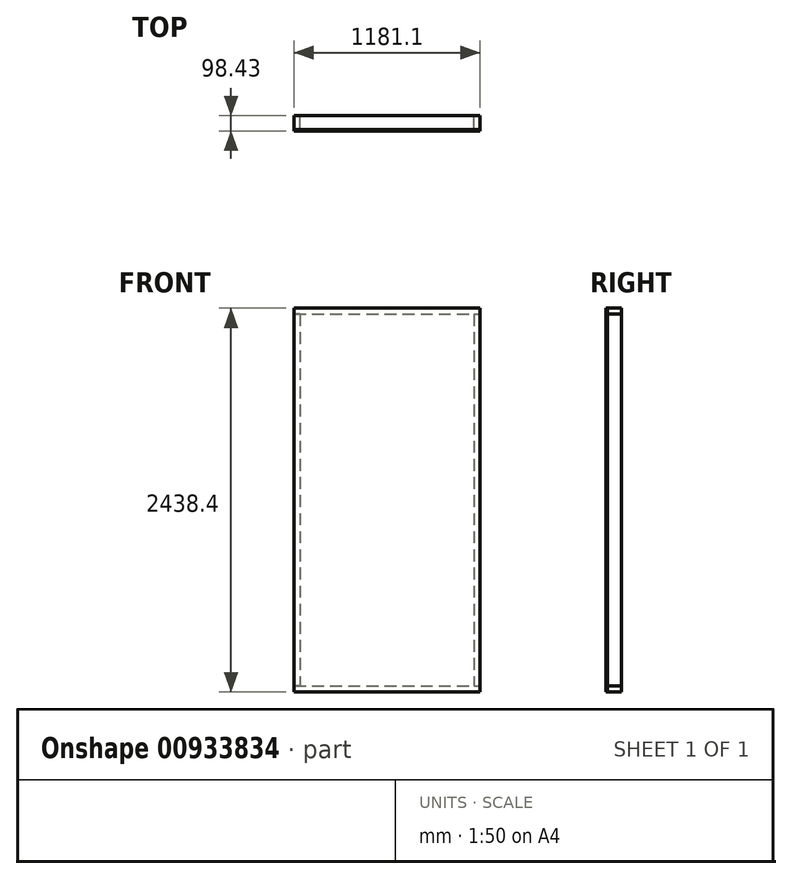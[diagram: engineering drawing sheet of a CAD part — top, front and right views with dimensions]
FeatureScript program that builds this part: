
annotation { "Feature Type Name" : "Feature", "Feature Type Description" : "" }
export const myFeature = defineFeature(function(context is Context, id is Id, definition is map)
    precondition{}
    {
        {
            var Q0;
            Q0=qCreatedBy(makeId("Front.planeOp"),FACE);
            var sketch = newSketch(context, id + "F0", { "sketchPlane" : qUnion([Q0])});
            skLineSegment(sketch, "E0.bottom", {"start": v(552.45, -1181.1) * mm, "end": v(-552.45, -1181.1) * mm, "construction": true});
            skLineSegment(sketch, "E0.top", {"start": v(552.45, 1181.1) * mm, "end": v(-552.45, 1181.1) * mm, "construction": true});
            skLineSegment(sketch, "E0.left", {"start": v(552.45, -1181.1) * mm, "end": v(552.45, 1181.1) * mm, "construction": true});
            skLineSegment(sketch, "E0.right", {"start": v(-552.45, -1181.1) * mm, "end": v(-552.45, 1181.1) * mm, "construction": true});
            skPoint(sketch, "E0.middle", {"position": v(0, 0) * mm});
            skLineSegment(sketch, "E1.bottom", {"start": v(-552.45, 1181.1) * mm, "end": v(-590.55, 1181.1) * mm});
            skLineSegment(sketch, "E1.top", {"start": v(-552.45, -1181.1) * mm, "end": v(-590.55, -1181.1) * mm});
            skLineSegment(sketch, "E1.left", {"start": v(-552.45, 1181.1) * mm, "end": v(-552.45, -1181.1) * mm});
            skLineSegment(sketch, "E1.right", {"start": v(-590.55, 1181.1) * mm, "end": v(-590.55, -1181.1) * mm});
            skLineSegment(sketch, "E2.bottom", {"start": v(552.45, 1181.1) * mm, "end": v(590.55, 1181.1) * mm});
            skLineSegment(sketch, "E2.top", {"start": v(552.45, -1181.1) * mm, "end": v(590.55, -1181.1) * mm});
            skLineSegment(sketch, "E2.left", {"start": v(552.45, 1181.1) * mm, "end": v(552.45, -1181.1) * mm});
            skLineSegment(sketch, "E2.right", {"start": v(590.55, 1181.1) * mm, "end": v(590.55, -1181.1) * mm});
            skLineSegment(sketch, "E3.bottom", {"start": v(-590.55, -1181.1) * mm, "end": v(590.55, -1181.1) * mm});
            skLineSegment(sketch, "E3.top", {"start": v(-590.55, -1219.2) * mm, "end": v(590.55, -1219.2) * mm});
            skLineSegment(sketch, "E3.left", {"start": v(-590.55, -1181.1) * mm, "end": v(-590.55, -1219.2) * mm});
            skLineSegment(sketch, "E3.right", {"start": v(590.55, -1181.1) * mm, "end": v(590.55, -1219.2) * mm});
            skLineSegment(sketch, "E4.bottom", {"start": v(-590.55, 1181.1) * mm, "end": v(590.55, 1181.1) * mm});
            skLineSegment(sketch, "E4.top", {"start": v(-590.55, 1219.2) * mm, "end": v(590.55, 1219.2) * mm});
            skLineSegment(sketch, "E4.left", {"start": v(-590.55, 1181.1) * mm, "end": v(-590.55, 1219.2) * mm});
            skLineSegment(sketch, "E4.right", {"start": v(590.55, 1181.1) * mm, "end": v(590.55, 1219.2) * mm});
            skLineSegment(sketch, "E5.bottom", {"start": v(-184.15, 1181.1) * mm, "end": v(-146.05, 1181.1) * mm});
            skLineSegment(sketch, "E5.top", {"start": v(-184.15, -1181.1) * mm, "end": v(-146.05, -1181.1) * mm});
            skLineSegment(sketch, "E5.left", {"start": v(-184.15, 1181.1) * mm, "end": v(-184.15, -1181.1) * mm});
            skLineSegment(sketch, "E5.right", {"start": v(-146.05, 1181.1) * mm, "end": v(-146.05, -1181.1) * mm});
            skLineSegment(sketch, "E6.bottom", {"start": v(0, 1181.1) * mm, "end": v(38.1, 1181.1) * mm});
            skLineSegment(sketch, "E6.top", {"start": v(0, -1181.1) * mm, "end": v(38.1, -1181.1) * mm});
            skLineSegment(sketch, "E7.bottom", {"start": v(222.25, 1181.1) * mm, "end": v(260.35, 1181.1) * mm});
            skLineSegment(sketch, "E7.top", {"start": v(222.25, -1181.1) * mm, "end": v(260.35, -1181.1) * mm});
            skLineSegment(sketch, "E7.left", {"start": v(222.25, 1181.1) * mm, "end": v(222.25, -1181.1) * mm});
            skLineSegment(sketch, "E7.right", {"start": v(260.35, 1181.1) * mm, "end": v(260.35, -1181.1) * mm});
            skSolve(sketch);
        }
        {
            var Q0;
            Q0=makeQuery(id+"F0.imprint","IMPRINT",FACE,{"disambiguationData":[TD([[makeQuery(id+"F0.imprint","IMPRINT",EDGE,{"derivedFrom":sQuery(id+"F0.wireOp",EDGE,"E4.top")}),-1.0]])]});
            var Q1;
            Q1=makeQuery(id+"F0.imprint","IMPRINT",FACE,{"disambiguationData":[TD([[makeQuery(id+"F0.imprint","IMPRINT",EDGE,{"derivedFrom":sQuery(id+"F0.wireOp",EDGE,"E3.top")}),1.0]])]});
            extrude(context, id + "F1", {"entities" : qUnion([Q0, Q1]), "endBound" : BoundingType.SYMMETRIC, "depth" : 88.9 * mm, "offsetDistance" : 25.4 * mm});
        }
        {
            var Q0;
            {var subQ0=sQuery(id+"F0.wireOp",EDGE,"E1.left");Q0=makeQuery(id+"F0.imprint","IMPRINT",FACE,{"disambiguationData":[TD([[makeQuery(id+"F0.imprint","IMPRINT",EDGE,{"derivedFrom":subQ0}),-1.0]])]});}
            var Q1;
            Q1=makeQuery(id+"F0.imprint","IMPRINT",FACE,{"disambiguationData":[TD([[makeQuery(id+"F0.imprint","IMPRINT",EDGE,{"derivedFrom":sQuery(id+"F0.wireOp",EDGE,"E5.bottom")}),-1.0]])]});
            var Q2;
            Q2=makeQuery(id+"F0.imprint","IMPRINT",FACE,{"disambiguationData":[TD([[makeQuery(id+"F0.imprint","IMPRINT",EDGE,{"derivedFrom":sQuery(id+"F0.wireOp",EDGE,"E7.bottom")}),-1.0]])]});
            var Q3;
            {var subQ0=sQuery(id+"F0.wireOp",EDGE,"E2.left");Q3=makeQuery(id+"F0.imprint","IMPRINT",FACE,{"disambiguationData":[TD([[makeQuery(id+"F0.imprint","IMPRINT",EDGE,{"derivedFrom":subQ0}),1.0]])]});}
            extrude(context, id + "F2", {"entities" : qUnion([Q0, Q1, Q2, Q3]), "endBound" : BoundingType.SYMMETRIC, "depth" : 88.9 * mm, "offsetDistance" : 25.4 * mm});
        }
        {
            var Q0;
            Q0=makeQuery(id+"F1.opExtrude","CAP_FACE",FACE,{"disambiguationData":[OSD([sQuery(id+"F0.wireOp",EDGE,"E4.bottom"),sQuery(id+"F0.wireOp",EDGE,"E4.top"),sQuery(id+"F0.wireOp",EDGE,"E4.left"),sQuery(id+"F0.wireOp",EDGE,"E4.right"),sQuery(id+"F0.wireOp",EDGE,"E5.bottom"),sQuery(id+"F0.wireOp",EDGE,"E6.bottom"),sQuery(id+"F0.wireOp",EDGE,"E7.bottom")])],"isStart":false});
            var sketch = newSketch(context, id + "F3", { "sketchPlane" : qUnion([Q0])});
            skLineSegment(sketch, "E8.bottom", {"start": v(-590.55, 1219.2) * mm, "end": v(590.55, 1219.2) * mm});
            skLineSegment(sketch, "E8.top", {"start": v(-590.55, -1219.2) * mm, "end": v(590.55, -1219.2) * mm});
            skLineSegment(sketch, "E8.left", {"start": v(-590.55, 1219.2) * mm, "end": v(-590.55, -1219.2) * mm});
            skLineSegment(sketch, "E8.right", {"start": v(590.55, 1219.2) * mm, "end": v(590.55, -1219.2) * mm});
            skSolve(sketch);
        }
        {
            var Q0;
            Q0 = qSketchRegion(id + "F3", true);
            extrude(context, id + "F4", {"entities" : qUnion([Q0]), "depth" : 9.52 * mm, "offsetDistance" : 25.4 * mm});
        }
    });
